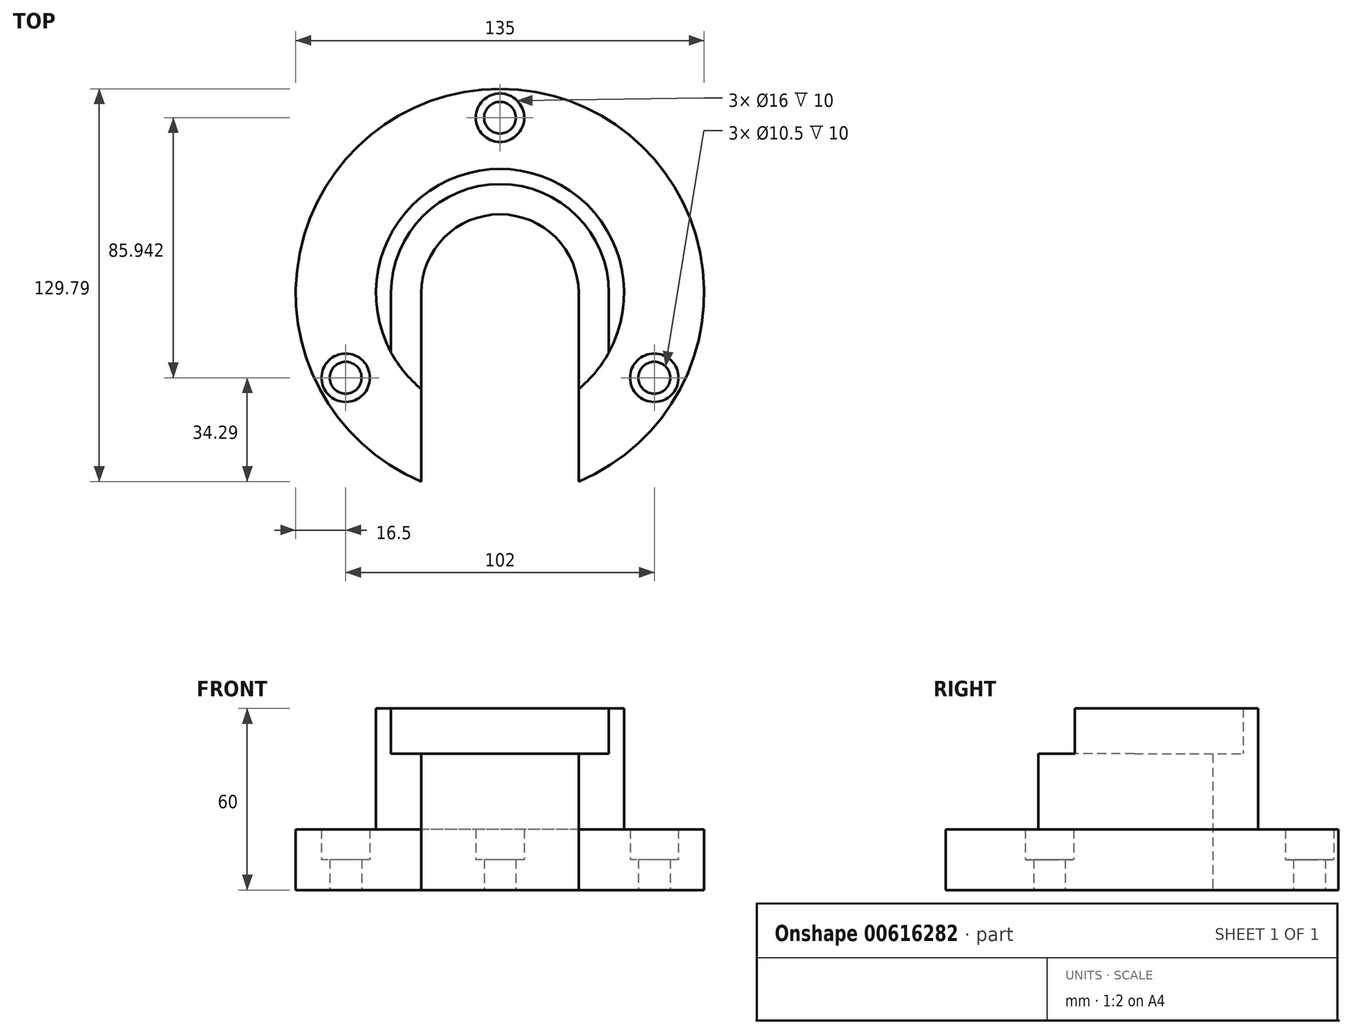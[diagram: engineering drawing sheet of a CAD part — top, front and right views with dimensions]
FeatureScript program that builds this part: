
annotation { "Feature Type Name" : "Feature", "Feature Type Description" : "" }
export const myFeature = defineFeature(function(context is Context, id is Id, definition is map)
    precondition{}
    {
        {
            var Q0;
            Q0=qCreatedBy(makeId("Top.planeOp"),FACE);
            var sketch = newSketch(context, id + "F0", { "sketchPlane" : qUnion([Q0])});
            skCircle(sketch, "E0", {"center": v(0, 0) * mm, "radius": 67.5 * mm});
            skCircle(sketch, "E1", {"center": v(0, 0) * mm, "radius": 26 * mm});
            skCircle(sketch, "E2", {"center": v(0, 0) * mm, "radius": 36 * mm});
            skCircle(sketch, "E3", {"center": v(0, 0) * mm, "radius": 41 * mm});
            skLineSegment(sketch, "E4", {"start": v(26, 0) * mm, "end": v(26, -62.3) * mm});
            skLineSegment(sketch, "E5", {"start": v(-26, 0) * mm, "end": v(-26, -62.3) * mm});
            skCircle(sketch, "E6", {"center": v(0, 57.94) * mm, "radius": 5.25 * mm});
            skCircle(sketch, "E7", {"center": v(51, -28) * mm, "radius": 5.25 * mm});
            skCircle(sketch, "E8", {"center": v(-51, -28) * mm, "radius": 5.25 * mm});
            skCircle(sketch, "E9", {"center": v(0, 57.94) * mm, "radius": 8 * mm});
            skCircle(sketch, "E10", {"center": v(-51, -28) * mm, "radius": 8 * mm});
            skCircle(sketch, "E11", {"center": v(51, -28) * mm, "radius": 8 * mm});
            skLineSegment(sketch, "E12", {"start": v(-36, 0) * mm, "end": v(-36, -19.62) * mm});
            skLineSegment(sketch, "E13", {"start": v(36, 0) * mm, "end": v(36, -19.62) * mm});
            skLineSegment(sketch, "E14", {"start": v(-26, -24.9) * mm, "end": v(-26, -31.7) * mm});
            skSolve(sketch);
        }
        {
            var Q0;
            Q0=makeQuery(id+"F0.imprint","IMPRINT",FACE,{"disambiguationData":[TD([[makeQuery(id+"F0.imprint","IMPRINT",EDGE,{"derivedFrom":sQuery(id+"F0.wireOp",EDGE,"E0")}),1.0]])]});
            var Q1;
            Q1=makeQuery(id+"F0.imprint","IMPRINT",FACE,{"disambiguationData":[TD([[makeQuery(id+"F0.imprint","IMPRINT",EDGE,{"derivedFrom":sQuery(id+"F0.wireOp",EDGE,"E2")}),-1.0]])]});
            var Q2;
            Q2=makeQuery(id+"F0.imprint","IMPRINT",FACE,{"disambiguationData":[TD([[makeQuery(id+"F0.imprint","IMPRINT",EDGE,{"derivedFrom":sQuery(id+"F0.wireOp",EDGE,"E1")}),-1.0]])]});
            extrude(context, id + "F1", {"entities" : qUnion([Q0, Q1, Q2]), "depth" : 60 * mm, "offsetDistance" : 25 * mm});
        }
        {
            var Q0;
            Q0=makeQuery(id+"F0.imprint","IMPRINT",FACE,{"disambiguationData":[TD([[makeQuery(id+"F0.imprint","IMPRINT",EDGE,{"derivedFrom":sQuery(id+"F0.wireOp",EDGE,"E0")}),1.0]])]});
            extrude(context, id + "F2", {"entities" : qUnion([Q0]), "operationType" : NewBodyOperationType.REMOVE, "depth" : 40 * mm, "offsetDistance" : 25 * mm});
        }
        {
            var Q0;
            {var subQ0=sQuery(id+"F0.wireOp",EDGE,"E4");var subQ1=sQuery(id+"F0.wireOp",EDGE,"E0");var subQ2=makeQuery(id+"F0.imprint","INTERSECT",VERTEX,{"derivedFrom":[subQ1,subQ0]});Q0=makeQuery(id+"F0.imprint","IMPRINT",FACE,{"disambiguationData":[TD([[makeQuery(id+"F0.imprint","IMPRINT",EDGE,{"disambiguationData":[TD([[subQ2,1.0]])],"derivedFrom":subQ1}),1.0]])]});}
            var Q1;
            {var subQ0=sQuery(id+"F0.wireOp",EDGE,"E4");var subQ1=sQuery(id+"F0.wireOp",EDGE,"E2");var subQ2=makeQuery(id+"F0.imprint","INTERSECT",VERTEX,{"derivedFrom":[subQ1,subQ0]});Q1=makeQuery(id+"F0.imprint","IMPRINT",FACE,{"disambiguationData":[TD([[makeQuery(id+"F0.imprint","IMPRINT",EDGE,{"disambiguationData":[TD([[subQ2,1.0]])],"derivedFrom":subQ1}),-1.0]])]});}
            var Q2;
            {var subQ0=sQuery(id+"F0.wireOp",EDGE,"E4");var subQ1=sQuery(id+"F0.wireOp",EDGE,"E1");var subQ2=makeQuery(id+"F0.imprint","INTERSECT",VERTEX,{"derivedFrom":[subQ1,subQ0]});Q2=makeQuery(id+"F0.imprint","IMPRINT",FACE,{"disambiguationData":[TD([[makeQuery(id+"F0.imprint","IMPRINT",EDGE,{"disambiguationData":[TD([[subQ2,1.0]])],"derivedFrom":subQ1}),-1.0]])]});}
            extrude(context, id + "F3", {"entities" : qUnion([Q0, Q1, Q2]), "operationType" : NewBodyOperationType.REMOVE, "endBound" : BoundingType.THROUGH_ALL, "depth" : 25 * mm, "offsetDistance" : 25 * mm});
        }
        {
            var Q0;
            Q0=makeQuery(id+"F0.imprint","IMPRINT",FACE,{"disambiguationData":[TD([[makeQuery(id+"F0.imprint","IMPRINT",EDGE,{"derivedFrom":sQuery(id+"F0.wireOp",EDGE,"E9")}),-1.0]])]});
            extrude(context, id + "F4", {"entities" : qUnion([Q0]), "operationType" : NewBodyOperationType.ADD, "depth" : 20 * mm, "offsetDistance" : 25 * mm});
        }
        {
            var Q0;
            Q0=makeQuery(id+"F0.imprint","IMPRINT",FACE,{"disambiguationData":[TD([[makeQuery(id+"F0.imprint","IMPRINT",EDGE,{"derivedFrom":sQuery(id+"F0.wireOp",EDGE,"E6")}),-1.0]])]});
            var Q1;
            Q1=makeQuery(id+"F0.imprint","IMPRINT",FACE,{"disambiguationData":[TD([[makeQuery(id+"F0.imprint","IMPRINT",EDGE,{"derivedFrom":sQuery(id+"F0.wireOp",EDGE,"E7")}),-1.0]])]});
            var Q2;
            Q2=makeQuery(id+"F0.imprint","IMPRINT",FACE,{"disambiguationData":[TD([[makeQuery(id+"F0.imprint","IMPRINT",EDGE,{"derivedFrom":sQuery(id+"F0.wireOp",EDGE,"E8")}),-1.0]])]});
            extrude(context, id + "F5", {"entities" : qUnion([Q0, Q1, Q2]), "operationType" : NewBodyOperationType.ADD, "depth" : 10 * mm, "offsetDistance" : 25 * mm});
        }
        {
            var Q0;
            Q0=qCreatedBy(makeId("Top.planeOp"),FACE);
            cPlane(context, id + "F6", {"entities" : qUnion([Q0]), "cplaneType" : CPlaneType.OFFSET, "offset" : 60 * mm, "width" : 150 * mm, "height" : 150 * mm});
        }
        {
            var Q0;
            Q0=qCreatedBy(id+"F6.planeOp",FACE);
            var sketch = newSketch(context, id + "F7", { "sketchPlane" : qUnion([Q0])});
            skCircle(sketch, "E15", {"center": v(0, 0) * mm, "radius": 36 * mm});
            skSolve(sketch);
        }
        {
            var Q0;
            {var subQ0=sQuery(id+"F7.wireOp",EDGE,"E15");var subQ1=makeQuery(id+"F7.imprint","IMPRINT",VERTEX,{"disambiguationData":[OD(0.0)],"derivedFrom":subQ0});Q0=makeQuery(id+"F7.imprint","IMPRINT",FACE,{"disambiguationData":[TD([[makeQuery(id+"F7.imprint","IMPRINT",EDGE,{"disambiguationData":[TD([[subQ1,1.0]])],"derivedFrom":subQ0}),1.0]])]});}
            extrude(context, id + "F8", {"entities" : qUnion([Q0]), "operationType" : NewBodyOperationType.REMOVE, "oppositeDirection" : true, "depth" : 15 * mm, "offsetDistance" : 25 * mm});
        }
        {
            var Q0;
            {var subQ5=sQuery(id+"F0.wireOp",EDGE,"E1");var subQ7=sQuery(id+"F0.wireOp",EDGE,"E4");var subQ9=makeQuery(id+"F0.imprint","INTERSECT",VERTEX,{"derivedFrom":[subQ5,subQ7]});Q0=makeQuery(id+"F0.imprint","IMPRINT",FACE,{"disambiguationData":[TD([[makeQuery(id+"F0.imprint","IMPRINT",EDGE,{"disambiguationData":[TD([[subQ9,-1.0]])],"derivedFrom":subQ5}),-1.0]])]});}
            extrude(context, id + "F9", {"entities" : qUnion([Q0]), "operationType" : NewBodyOperationType.ADD, "depth" : 45 * mm, "offsetDistance" : 25 * mm});
        }
        {
            var Q0;
            Q0=makeQuery(id+"F1.opExtrude","CAP_FACE",FACE,{"disambiguationData":[OSD([sQuery(id+"F0.wireOp",EDGE,"E0"),sQuery(id+"F0.wireOp",EDGE,"E1"),sQuery(id+"F0.wireOp",EDGE,"E2"),sQuery(id+"F0.wireOp",EDGE,"E3"),sQuery(id+"F0.wireOp",EDGE,"E4"),sQuery(id+"F0.wireOp",EDGE,"E5")])],"isStart":false});
            var sketch = newSketch(context, id + "F10", { "sketchPlane" : qUnion([Q0])});
            skLineSegment(sketch, "E16", {"start": v(-36, 0) * mm, "end": v(-36, -19.62) * mm});
            skLineSegment(sketch, "E17", {"start": v(-26, -24.9) * mm, "end": v(-26, -31.7) * mm});
            skLineSegment(sketch, "E18", {"start": v(36, 0) * mm, "end": v(36, -19.62) * mm});
            skLineSegment(sketch, "E19", {"start": v(26, -24.9) * mm, "end": v(26, -31.7) * mm});
            skArc(sketch, "E20", {"start": v(-36, 0) * mm, "mid": v(-33.4, -13.42) * mm, "end": v(-26, -24.9) * mm});
            skSolve(sketch);
        }
        {
            var Q0;
            {var subQ0=sQuery(id+"F10.wireOp",EDGE,"E16");Q0=makeQuery(id+"F10.imprint","IMPRINT",FACE,{"disambiguationData":[TD([[makeQuery(id+"F10.imprint","IMPRINT",EDGE,{"derivedFrom":subQ0}),1.0]])]});}
            var Q1;
            {var subQ0=sQuery(id+"F10.wireOp",EDGE,"E18");Q1=makeQuery(id+"F10.imprint","IMPRINT",FACE,{"disambiguationData":[TD([[makeQuery(id+"F10.imprint","IMPRINT",EDGE,{"derivedFrom":subQ0}),-1.0]])]});}
            extrude(context, id + "F11", {"entities" : qUnion([Q0, Q1]), "operationType" : NewBodyOperationType.REMOVE, "oppositeDirection" : true, "depth" : 15 * mm, "offsetDistance" : 25 * mm});
        }
    });
